# Revit family: Kabelrinnen-Systeme_Magic_Kabelrinne_RKS-Magic
name_source: partatom
category: Generic Models
revit_build: Autodesk Revit 2015 (Build: 20140606_1530(x64)
units: mm (PartAtom-declared; Revit-internal decimal feet)

## types (15) — shared parameters
Manufacturer = OBO Bettermann
Material = Steel, Galvanized
URL = http://www.obo-bettermann.com

## per-type parameters (varying)
| type | "B" Dimension | GTIN | H | Manufacturer Art. No. |
| RKSM 330 FS | 300 mm | 4012195390862 | 35 mm | 6047460 |
| RKSM 320 FS | 200 mm  [stored 0.656168 ft] | 4012195390855 | 35 mm | 6047433 |
| RKSM 310 FS | 100 mm  [stored 0.328084 ft] | 4012195390848 | 35 mm | 6047417 |
| RKSM 610 FS | 100 mm  [stored 0.328084 ft] | 4012195390879 | 60 mm  [stored 0.19685 ft] | 6047611 |
| RKSM 615 FS | 150 mm | 4012195391197 | 60 mm  [stored 0.19685 ft] | 6047630 |
| RKSM 620 FS | 200 mm  [stored 0.656168 ft] | 4012195391203 | 60 mm  [stored 0.19685 ft] | 6047638 |
| RKSM 630 FS | 300 mm | 4012195391210 | 60 mm  [stored 0.19685 ft] | 6047654 |
| RKSM 640 FS | 400 mm  [stored 1.31234 ft] | 4012195391227 | 60 mm  [stored 0.19685 ft] | 6047689 |
| RKSM 650 FS | 500 mm  [stored 1.64042 ft] | 4012195391234 | 60 mm  [stored 0.19685 ft] | 6047719 |
| RKSM 660 FS | 600 mm | 4012195391241 | 60 mm  [stored 0.19685 ft] | 6047735 |
| RKSM 610 FT | 100 mm  [stored 0.328084 ft] | 4012195903895 | 60 mm  [stored 0.19685 ft] | 6047612 |
| RKSM 615 FT | 150 mm | 4012195903901 | 60 mm  [stored 0.19685 ft] | 6047631 |
| RKSM 620 FT | 200 mm  [stored 0.656168 ft] | 4012195903932 | 60 mm  [stored 0.19685 ft] | 6047639 |
| RKSM 630 FT | 300 mm | 4012195903949 | 60 mm  [stored 0.19685 ft] | 6047655 |
| RKSM 640 FT | 400 mm  [stored 1.31234 ft] | 4012195903956 | 60 mm  [stored 0.19685 ft] | 6047690 |

note: column(s) folded — value = type name in every type: Article Type

note: [stored X ft] marks values corroborated as IEEE doubles in the binary element streams (Revit-internal decimal feet)

## geometry (parser evidence)
native form markers: Sweep x2
no freeform markers — native parametric forms only
